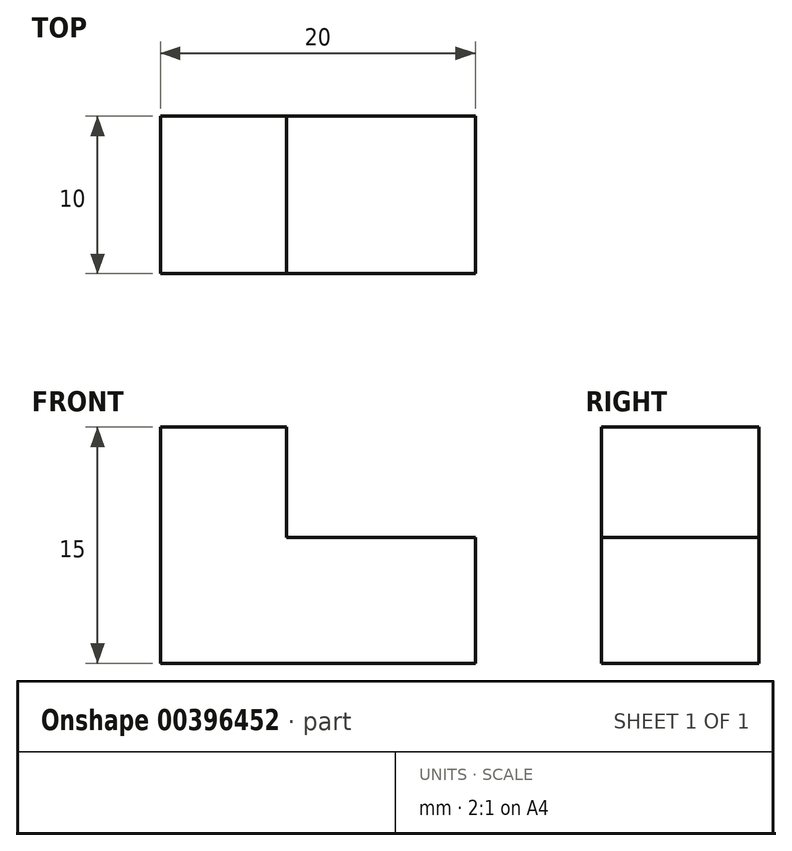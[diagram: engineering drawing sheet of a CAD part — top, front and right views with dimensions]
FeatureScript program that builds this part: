
annotation { "Feature Type Name" : "Feature", "Feature Type Description" : "" }
export const myFeature = defineFeature(function(context is Context, id is Id, definition is map)
    precondition{}
    {
        {
            var Q0;
            Q0=qCreatedBy(makeId("Front.planeOp"),FACE);
            var sketch = newSketch(context, id + "F0", { "sketchPlane" : qUnion([Q0])});
            skLineSegment(sketch, "E0", {"start": v(0, 15) * mm, "end": v(0, 0) * mm});
            skLineSegment(sketch, "E1", {"start": v(0, 0) * mm, "end": v(20, 0) * mm});
            skLineSegment(sketch, "E2", {"start": v(20, 0) * mm, "end": v(20, 8) * mm});
            skLineSegment(sketch, "E3", {"start": v(20, 8) * mm, "end": v(8, 8) * mm});
            skLineSegment(sketch, "E4", {"start": v(8, 8) * mm, "end": v(8, 15) * mm});
            skLineSegment(sketch, "E5", {"start": v(8, 15) * mm, "end": v(0, 15) * mm});
            skSolve(sketch);
        }
        {
            var Q0;
            Q0=makeQuery(id+"F0.imprint","IMPRINT",FACE,{"disambiguationData":[TD([[makeQuery(id+"F0.imprint","IMPRINT",EDGE,{"derivedFrom":sQuery(id+"F0.wireOp",EDGE,"E0")}),1.0]])]});
            extrude(context, id + "F1", {"entities" : qUnion([Q0]), "depth" : 10 * mm});
        }
    });
